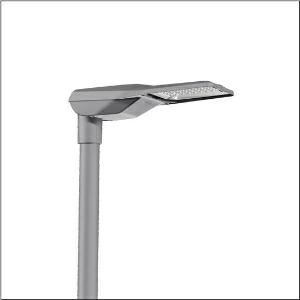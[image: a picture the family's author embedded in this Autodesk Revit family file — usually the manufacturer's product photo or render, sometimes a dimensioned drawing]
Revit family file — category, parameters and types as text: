
# Revit family: streetlight_sl_21_iq_mini___stw1_0a_5xe2e31d08jb_eadb
name_source: partatom
category: Lighting Fixtures
units: mm (PartAtom-declared; Revit-internal decimal feet)

## family parameters
Cut with Voids When Loaded = No
Host = Face
Light Source = No
Part Type = Normal
Room Calculation Point = No
Round Connector Dimension = Use Diameter
Shared = No

## types (1)
- --- (1 x LED, 10820 lm, 71.6 W, 3000K)
    Apparent Load = 72 VA
    CIE Flux Codes = 39 75 98 100 100
    Color Rendering = 70
    Color Temperature = 3000K
    Default Elevation = 1800 mm
    Description = Streetlight SL 21 iQ mini, mast luminaire, primary light control with lens, of PMMA, primary optical cover: cover, of toughened safety glass, transparent, light distribution: STW1.0a, light emission: direct distribution, primary light characteristic: asymmetric, installation type: post-top, side-entry, LED, High Power LED, rated luminous flux: 10.820lm, luminous efficacy: 151lm/W, light colour: 730, colour temperature: 3000K, control: Auto-Match, Temp-Guard, Lumen-Switch, Night-Set, Smart-Wire, Light-Fading, Desk-Remote (wireless, voltage-free reading and setting of iQ features in the workshop via application-optimized NFC function/RFID function), optimised constant luminous flux control (CLO 2.0), presetting dimming linear, mains connection: 220..240V, AC, 50/60Hz, start of lifetime: 72W, end of service life: 75W, reduction: 33W, luminaire housing, of diecast aluminium, powder-coated, Siteco® metallic grey (DB 702S), corrosivity category C5 mid according to DIN EN ISO 12944, please order mast flange separately, inclination adjustable: 0°, 5°, 10°, 15°, sealing non-destructively replaceable, multi-level sealing system, length: 628mm, width: 235mm, height: 110mm, mast flange for spigot size: 42mm (side-entry): 5XC10008XM4, 60/48mm (side-entry/post-top): 5XC10108XM2, 76/60mm (side-entry/post-top): 5XC10108XM1, protection rating (complete): IP66, insulation class (complete): insulation class II (safety insulation), certification: CE, ENEC, ENEC+, VDE, impact resistance: IK09, permissible operating ambient temperature for outdoor applications: -40..+50°C, standard-compliant lighting for roads and squares, packaging unit: 1 piece

Light Distribution: STW1.0a
    Height = 110 mm
    Lamp = 1 x LED
    Lamp Light Flux = 10820 lm
    Lamp Power = 71.6 W
    Lamp count = 1
    Length = 625 mm
    Luminous efficacy = 151 lm/W
    Manufacturer = Siteco
    ModVariant = No
    Model = 5XE2E31D08JB
    Number of Poles = 1
    OnlyDefault = Yes
    Power Factor = 1
    Product Name = Streetlight SL 21 iQ mini | STW1.0a
    Product group = mast luminaire | pylon top
    ProductGroupID = 6100
    Protection Class = Protection class II
    Protection Degree = IP 66
    RLX_Detail_Level = 1
    RLX_Emergency_Light_Flux = 0 lm
    RLX_Emergency_Type = 0
    RLX_Emergency_Type_DB = No
    RlxData = <blob elided: 92373 chars, md5=05bdd0d1>
    Socket = socket
    Standby Power = 0 W
    System Light Flux = 10820 lm
    System Power = 72 W
    Type Comments = factory setting: luminous flux: 100 % | dim-lin: 254 | 746 mA
    Type Image = l_1003519.jpg
    URL = http://relux.com
    VarID = @adj_102967
    Voltage = 0 V
    Weight = 0.00 kg
    Width = 234 mm

## geometry (parser evidence)
native form markers: Blend x4, Sweep x12
no freeform markers — native parametric forms only
